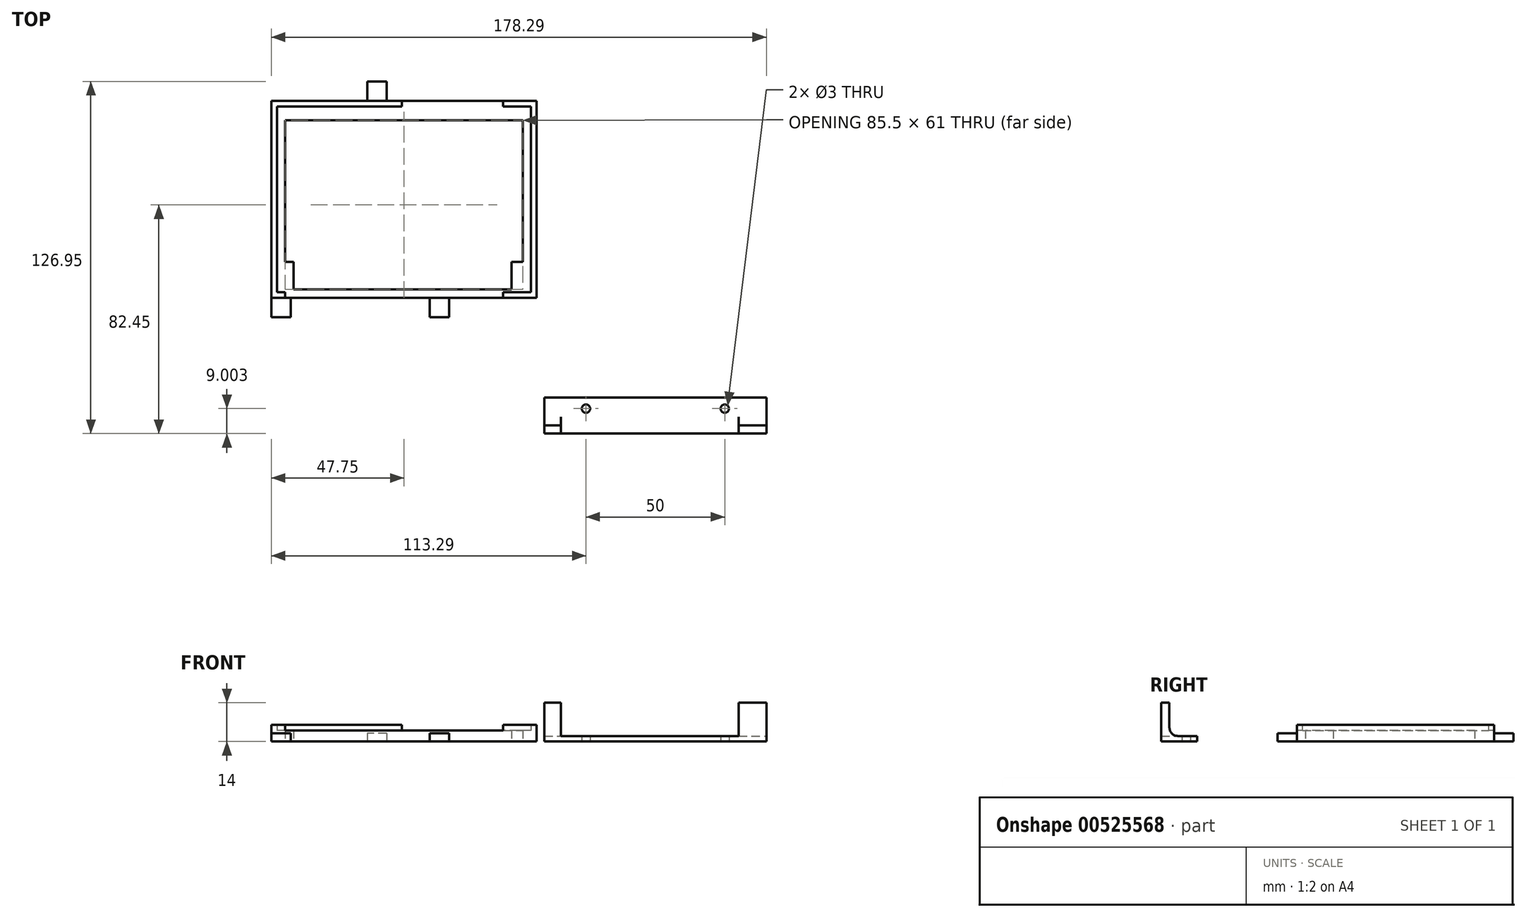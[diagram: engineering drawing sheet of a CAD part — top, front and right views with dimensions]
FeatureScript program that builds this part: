
annotation { "Feature Type Name" : "Feature", "Feature Type Description" : "" }
export const myFeature = defineFeature(function(context is Context, id is Id, definition is map)
    precondition{}
    {
        {
            var Q0;
            Q0=qCreatedBy(makeId("Top.planeOp"),FACE);
            var sketch = newSketch(context, id + "F0", { "sketchPlane" : qUnion([Q0])});
            skLineSegment(sketch, "E0.bottom", {"start": v(45.75, -33.5) * mm, "end": v(-45.75, -33.5) * mm});
            skLineSegment(sketch, "E0.top", {"start": v(45.75, 33.5) * mm, "end": v(-45.75, 33.5) * mm});
            skLineSegment(sketch, "E0.left", {"start": v(45.75, -33.5) * mm, "end": v(45.75, 33.5) * mm});
            skLineSegment(sketch, "E0.right", {"start": v(-45.75, -33.5) * mm, "end": v(-45.75, 33.5) * mm});
            skPoint(sketch, "E0.middle", {"position": v(0, 0) * mm});
            skLineSegment(sketch, "E1.bottom", {"start": v(47.75, -35.5) * mm, "end": v(-47.75, -35.5) * mm});
            skLineSegment(sketch, "E1.top", {"start": v(47.75, 35.5) * mm, "end": v(-47.75, 35.5) * mm});
            skLineSegment(sketch, "E1.left", {"start": v(47.75, -35.5) * mm, "end": v(47.75, 35.5) * mm});
            skLineSegment(sketch, "E1.right", {"start": v(-47.75, -35.5) * mm, "end": v(-47.75, 35.5) * mm});
            skSolve(sketch);
        }
        {
            var Q0;
            Q0=qSketchRegion(id+"F0",true);
            extrude(context, id + "F1", {"entities" : qUnion([Q0]), "depth" : 6 * mm, "offsetDistance" : 25 * mm});
        }
        {
            var Q0;
            Q0=makeQuery(id+"F1.opExtrude","CAP_FACE",FACE,{"disambiguationData":[OSD([sQuery(id+"F0.wireOp",EDGE,"E0.bottom"),sQuery(id+"F0.wireOp",EDGE,"E0.top"),sQuery(id+"F0.wireOp",EDGE,"E0.left"),sQuery(id+"F0.wireOp",EDGE,"E0.right"),sQuery(id+"F0.wireOp",EDGE,"E1.bottom"),sQuery(id+"F0.wireOp",EDGE,"E1.top"),sQuery(id+"F0.wireOp",EDGE,"E1.left"),sQuery(id+"F0.wireOp",EDGE,"E1.right")])],"isStart":true});
            var sketch = newSketch(context, id + "F2", { "sketchPlane" : qUnion([Q0])});
            skLineSegment(sketch, "E2.bottom", {"start": v(45.75, 33.5) * mm, "end": v(-45.75, 33.5) * mm});
            skLineSegment(sketch, "E2.top", {"start": v(45.75, -33.5) * mm, "end": v(-45.75, -33.5) * mm});
            skLineSegment(sketch, "E2.left", {"start": v(45.75, 33.5) * mm, "end": v(45.75, -33.5) * mm});
            skLineSegment(sketch, "E2.right", {"start": v(-45.75, 33.5) * mm, "end": v(-45.75, -33.5) * mm});
            skPoint(sketch, "E2.middle", {"position": v(0, 0) * mm});
            skLineSegment(sketch, "E3.bottom", {"start": v(-42.75, -28.5) * mm, "end": v(-30.75, -28.5) * mm});
            skLineSegment(sketch, "E3.top", {"start": v(-39.75, 32.5) * mm, "end": v(38.75, 32.5) * mm});
            skLineSegment(sketch, "E3.left", {"start": v(-42.75, -28.5) * mm, "end": v(-42.75, 22.5) * mm});
            skLineSegment(sketch, "E3.right", {"start": v(42.75, -28.5) * mm, "end": v(42.75, 22.5) * mm});
            skLineSegment(sketch, "E4", {"start": v(42.75, 22.5) * mm, "end": v(38.75, 22.5) * mm});
            skLineSegment(sketch, "E5", {"start": v(38.75, 22.5) * mm, "end": v(38.75, 32.5) * mm});
            skLineSegment(sketch, "E6", {"start": v(-30.75, -28.5) * mm, "end": v(-30.75, -28.5) * mm});
            skLineSegment(sketch, "E7", {"start": v(-30.75, -28.5) * mm, "end": v(-20.75, -28.5) * mm});
            skLineSegment(sketch, "E8", {"start": v(-20.75, -28.5) * mm, "end": v(-20.75, -28.5) * mm});
            skLineSegment(sketch, "E9.trimOffspring", {"start": v(-20.75, -28.5) * mm, "end": v(42.75, -28.5) * mm});
            skLineSegment(sketch, "E10", {"start": v(-42.75, 22.5) * mm, "end": v(-39.75, 22.5) * mm});
            skLineSegment(sketch, "E11", {"start": v(-39.75, 22.5) * mm, "end": v(-39.75, 32.5) * mm});
            skSolve(sketch);
        }
        {
            var Q0;
            Q0=qSketchRegion(id+"F2",true);
            extrude(context, id + "F3", {"entities" : qUnion([Q0]), "operationType" : NewBodyOperationType.ADD, "oppositeDirection" : true, "depth" : 4 * mm, "offsetDistance" : 25 * mm});
        }
        {
            var Q0;
            Q0=makeQuery(id+"F1.opExtrude","CAP_FACE",FACE,{"disambiguationData":[OSD([sQuery(id+"F0.wireOp",EDGE,"E0.bottom"),sQuery(id+"F0.wireOp",EDGE,"E0.top"),sQuery(id+"F0.wireOp",EDGE,"E0.left"),sQuery(id+"F0.wireOp",EDGE,"E0.right"),sQuery(id+"F0.wireOp",EDGE,"E1.bottom"),sQuery(id+"F0.wireOp",EDGE,"E1.top"),sQuery(id+"F0.wireOp",EDGE,"E1.left"),sQuery(id+"F0.wireOp",EDGE,"E1.right")])],"isStart":false});
            var sketch = newSketch(context, id + "F4", { "sketchPlane" : qUnion([Q0])});
            skLineSegment(sketch, "E12.bottom", {"start": v(-42.75, -33.5) * mm, "end": v(35.75, -33.5) * mm});
            skLineSegment(sketch, "E12.top", {"start": v(-42.75, -35.5) * mm, "end": v(35.75, -35.5) * mm});
            skLineSegment(sketch, "E12.left", {"start": v(-42.75, -33.5) * mm, "end": v(-42.75, -35.5) * mm});
            skLineSegment(sketch, "E12.right", {"start": v(35.75, -33.5) * mm, "end": v(35.75, -35.5) * mm});
            skLineSegment(sketch, "E13.bottom", {"start": v(-0.75, 35.5) * mm, "end": v(35.75, 35.5) * mm});
            skLineSegment(sketch, "E13.top", {"start": v(-0.75, 33.5) * mm, "end": v(35.75, 33.5) * mm});
            skLineSegment(sketch, "E13.left", {"start": v(-0.75, 35.5) * mm, "end": v(-0.75, 33.5) * mm});
            skLineSegment(sketch, "E13.right", {"start": v(35.75, 35.5) * mm, "end": v(35.75, 33.5) * mm});
            skSolve(sketch);
        }
        {
            var Q0;
            Q0=qSketchRegion(id+"F4",true);
            extrude(context, id + "F5", {"entities" : qUnion([Q0]), "operationType" : NewBodyOperationType.REMOVE, "oppositeDirection" : true, "depth" : 2 * mm, "offsetDistance" : 25 * mm});
        }
        {
            var Q0;
            Q0=makeQuery(id+"F3.boolean.opBoolean","MERGE",FACE,{"derivedFrom":[makeQuery(id+"F1.opExtrude","CAP_FACE",FACE,{"disambiguationData":[OSD([sQuery(id+"F0.wireOp",EDGE,"E0.bottom"),sQuery(id+"F0.wireOp",EDGE,"E0.top"),sQuery(id+"F0.wireOp",EDGE,"E0.left"),sQuery(id+"F0.wireOp",EDGE,"E0.right"),sQuery(id+"F0.wireOp",EDGE,"E1.bottom"),sQuery(id+"F0.wireOp",EDGE,"E1.top"),sQuery(id+"F0.wireOp",EDGE,"E1.left"),sQuery(id+"F0.wireOp",EDGE,"E1.right")])],"isStart":true}),makeQuery(id+"F3.opExtrude","CAP_FACE",FACE,{"disambiguationData":[OSD([sQuery(id+"F2.wireOp",EDGE,"E2.bottom"),sQuery(id+"F2.wireOp",EDGE,"E2.top"),sQuery(id+"F2.wireOp",EDGE,"E2.left"),sQuery(id+"F2.wireOp",EDGE,"E2.right"),sQuery(id+"F2.wireOp",EDGE,"E3.bottom"),sQuery(id+"F2.wireOp",EDGE,"E3.top"),sQuery(id+"F2.wireOp",EDGE,"E3.left"),sQuery(id+"F2.wireOp",EDGE,"E3.right"),sQuery(id+"F2.wireOp",EDGE,"E4"),sQuery(id+"F2.wireOp",EDGE,"E5"),sQuery(id+"F2.wireOp",EDGE,"E6"),sQuery(id+"F2.wireOp",EDGE,"E7"),sQuery(id+"F2.wireOp",EDGE,"E8"),sQuery(id+"F2.wireOp",EDGE,"E9.trimOffspring")])],"isStart":true})]});
            var sketch = newSketch(context, id + "F6", { "sketchPlane" : qUnion([Q0])});
            skLineSegment(sketch, "E14.bottom", {"start": v(-47.75, 35.5) * mm, "end": v(-40.75, 35.5) * mm});
            skLineSegment(sketch, "E14.top", {"start": v(-47.75, 42.5) * mm, "end": v(-40.75, 42.5) * mm});
            skLineSegment(sketch, "E14.left", {"start": v(-47.75, 35.5) * mm, "end": v(-47.75, 42.5) * mm});
            skLineSegment(sketch, "E14.right", {"start": v(-40.75, 35.5) * mm, "end": v(-40.75, 42.5) * mm});
            skCircle(sketch, "E15", {"center": v(-44.25, 39) * mm, "radius": 1.5 * mm, "construction": true});
            skPoint(sketch, "E15.centerSnap0", {"position": v(-47.75, 39) * mm});
            skPoint(sketch, "E15.centerSnap1", {"position": v(-44.25, 35.5) * mm});
            skLineSegment(sketch, "E16.bottom", {"start": v(-13.25, -35.5) * mm, "end": v(-6.25, -35.5) * mm});
            skLineSegment(sketch, "E16.top", {"start": v(-13.25, -42.5) * mm, "end": v(-6.25, -42.5) * mm});
            skLineSegment(sketch, "E16.left", {"start": v(-13.25, -35.5) * mm, "end": v(-13.25, -42.5) * mm});
            skLineSegment(sketch, "E16.right", {"start": v(-6.25, -35.5) * mm, "end": v(-6.25, -42.5) * mm});
            skCircle(sketch, "E17", {"center": v(-9.75, -39) * mm, "radius": 1.5 * mm, "construction": true});
            skPoint(sketch, "E17.centerSnap0", {"position": v(-9.75, -42.5) * mm});
            skPoint(sketch, "E17.centerSnap1", {"position": v(-13.25, -39) * mm});
            skLineSegment(sketch, "E18.bottom", {"start": v(16.25, 35.5) * mm, "end": v(9.25, 35.5) * mm});
            skLineSegment(sketch, "E18.top", {"start": v(16.25, 42.5) * mm, "end": v(9.25, 42.5) * mm});
            skLineSegment(sketch, "E18.left", {"start": v(16.25, 35.5) * mm, "end": v(16.25, 42.5) * mm});
            skLineSegment(sketch, "E18.right", {"start": v(9.25, 35.5) * mm, "end": v(9.25, 42.5) * mm});
            skCircle(sketch, "E19", {"center": v(12.75, 39) * mm, "radius": 1.5 * mm, "construction": true});
            skPoint(sketch, "E19.centerSnap0", {"position": v(12.75, 35.5) * mm});
            skPoint(sketch, "E19.centerSnap1", {"position": v(9.25, 39) * mm});
            skSolve(sketch);
        }
        {
            var Q0;
            Q0=qSketchRegion(id+"F6",true);
            extrude(context, id + "F7", {"entities" : qUnion([Q0]), "operationType" : NewBodyOperationType.ADD, "oppositeDirection" : true, "depth" : 3 * mm, "offsetDistance" : 25 * mm});
        }
        {
            var Q0;
            Q0=qCreatedBy(makeId("Top.planeOp"),FACE);
            var sketch = newSketch(context, id + "F8", { "sketchPlane" : qUnion([Q0])});
            skLineSegment(sketch, "E20.bottom", {"start": v(130.54, -84.45) * mm, "end": v(50.54, -84.45) * mm});
            skLineSegment(sketch, "E20.top", {"start": v(130.54, -71.45) * mm, "end": v(50.54, -71.45) * mm});
            skLineSegment(sketch, "E20.left", {"start": v(130.54, -84.45) * mm, "end": v(130.54, -71.45) * mm});
            skLineSegment(sketch, "E20.right", {"start": v(50.54, -84.45) * mm, "end": v(50.54, -71.45) * mm});
            skPoint(sketch, "E20.middle", {"position": v(90.54, -77.95) * mm});
            skCircle(sketch, "E21", {"center": v(65.54, -75.45) * mm, "radius": 1.5 * mm});
            skCircle(sketch, "E22", {"center": v(115.54, -75.45) * mm, "radius": 1.5 * mm});
            skSolve(sketch);
        }
        {
            var Q0;
            Q0=qSketchRegion(id+"F8",true);
            extrude(context, id + "F9", {"entities" : qUnion([Q0]), "depth" : 2 * mm, "offsetDistance" : 25 * mm});
        }
        {
            var Q0;
            Q0=makeQuery(id+"F9.opExtrude","SWEPT_FACE",FACE,{"disambiguationData":[OSD([sQuery(id+"F8.wireOp",EDGE,"E20.bottom")])]});
            var sketch = newSketch(context, id + "F10", { "sketchPlane" : qUnion([Q0])});
            skLineSegment(sketch, "E23.bottom", {"start": v(120.54, 0) * mm, "end": v(130.54, 0) * mm});
            skLineSegment(sketch, "E23.top", {"start": v(120.54, 14) * mm, "end": v(130.54, 14) * mm});
            skLineSegment(sketch, "E23.left", {"start": v(130.54, 0) * mm, "end": v(130.54, 14) * mm});
            skLineSegment(sketch, "E23.right", {"start": v(120.54, 0) * mm, "end": v(120.54, 14) * mm});
            skLineSegment(sketch, "E24.bottom", {"start": v(50.54, 0) * mm, "end": v(56.54, 0) * mm});
            skLineSegment(sketch, "E24.top", {"start": v(50.54, 14) * mm, "end": v(56.54, 14) * mm});
            skLineSegment(sketch, "E24.left", {"start": v(50.54, 0) * mm, "end": v(50.54, 14) * mm});
            skLineSegment(sketch, "E24.right", {"start": v(56.54, 0) * mm, "end": v(56.54, 14) * mm});
            skSolve(sketch);
        }
        {
            var Q0;
            Q0=qSketchRegion(id+"F10",true);
            extrude(context, id + "F11", {"entities" : qUnion([Q0]), "operationType" : NewBodyOperationType.ADD, "oppositeDirection" : true, "depth" : 3 * mm, "offsetDistance" : 25 * mm});
        }
        {
            var Q0;
            Q0=makeQuery(id+"F11.boolean.opBoolean","INTERSECT",EDGE,{"derivedFrom":[makeQuery(id+"F9.opExtrude","CAP_FACE",FACE,{"disambiguationData":[OSD([sQuery(id+"F8.wireOp",EDGE,"E20.bottom"),sQuery(id+"F8.wireOp",EDGE,"E20.top"),sQuery(id+"F8.wireOp",EDGE,"E20.left"),sQuery(id+"F8.wireOp",EDGE,"E20.right"),sQuery(id+"F8.wireOp",EDGE,"E21"),sQuery(id+"F8.wireOp",EDGE,"E22")])],"isStart":false}),makeQuery(id+"F11.opExtrude","CAP_FACE",FACE,{"disambiguationData":[OSD([sQuery(id+"F10.wireOp",EDGE,"E24.bottom"),sQuery(id+"F10.wireOp",EDGE,"E24.top"),sQuery(id+"F10.wireOp",EDGE,"E24.left"),sQuery(id+"F10.wireOp",EDGE,"E24.right")])],"isStart":false})]});
            var Q1;
            Q1=makeQuery(id+"F11.boolean.opBoolean","INTERSECT",EDGE,{"derivedFrom":[makeQuery(id+"F9.opExtrude","CAP_FACE",FACE,{"disambiguationData":[OSD([sQuery(id+"F8.wireOp",EDGE,"E20.bottom"),sQuery(id+"F8.wireOp",EDGE,"E20.top"),sQuery(id+"F8.wireOp",EDGE,"E20.left"),sQuery(id+"F8.wireOp",EDGE,"E20.right"),sQuery(id+"F8.wireOp",EDGE,"E21"),sQuery(id+"F8.wireOp",EDGE,"E22")])],"isStart":false}),makeQuery(id+"F11.opExtrude","CAP_FACE",FACE,{"disambiguationData":[OSD([sQuery(id+"F10.wireOp",EDGE,"E23.bottom"),sQuery(id+"F10.wireOp",EDGE,"E23.top"),sQuery(id+"F10.wireOp",EDGE,"E23.left"),sQuery(id+"F10.wireOp",EDGE,"E23.right")])],"isStart":false})]});
            fillet(context, id + "F12", {"entities" : qUnion([Q0, Q1]), "radius" : 3 * mm, "tangentPropagation" : true, "allowEdgeOverflow" : false});
        }
    });
